# Revit family: ACV Standard Series
name_source: partatom
category: Generic Models
revit_build: Autodesk Revit 2014 (Build: 20130308_1515(x64)
units: mm (PartAtom-declared; Revit-internal decimal feet)

## types (16) — shared parameters
9rp = 9.47 "
Description = BEECO ACV Standard Series
MATERIAL = Iron, Cast
Manufacturer = MIFAB
URL = www.mifab.com

## per-type parameters (varying)
- ACV1.50: 10Hole=0.19 "; 10rp=1.43 "; 1RADIUS=1 "; 1height=0.5 "; 1rib thk=0.21 "; 2radi=2.55 "; 2radi2=1.79 "; 2ribrad=0.05 "; 2ribthk=0.11 "; 3Radius=2 "; 4Height=0.64 "; 4Thk=0.04 "; 5Height=0.9 "; 5inside=0.46 "; 6Outside=0.27 "; 6inside=0.19 "; 6inside2=2.85 "; 7height=0.9 "; 7rp=1.98 "; 7width=0.45 "; 8 HOLE DIST=2.32 "; 8HOLE=0.08 "; 9 HOLE RAD=1.13 "; 9Hole=0.11 "; CutID=0.49 "; Dia.=1.5 "; H=7.31 "; L=9.06 "; R=3.25 "; R RADIUS=0.3 "; R THK=2 "; Radius=0.75 "; W=6 "; W/2=3 "; l1=1.08 "
- ACV2.00: 10Hole=0.25 "; 10rp=1.9 "; 1RADIUS=1.25 "; 1height=0.5 "; 1rib thk=0.29 "; 2radi=2.55 "; 2radi2=1.79 "; 2ribrad=0.05 "; 2ribthk=0.15 "; 3Radius=1.5 "; 4Height=0.85 "; 4Thk=0.05 "; 5Height=1.2 "; 5inside=0.46 "; 6Outside=0.36 "; 6inside=0.25 "; 6inside2=2.75 "; 7height=1.2 "; 7rp=1.94 "; 7width=0.6 "; 8 HOLE DIST=2.32 "; 8HOLE=0.1 "; 9 HOLE RAD=1.5 "; 9Hole=0.15 "; CutID=0.65 "; Dia.=2 "; H=7.31 "; L=9.06 "; R=3.25 "; R RADIUS=0.4 "; R THK=2 "; Radius=1 "; W=6 "; W/2=3 "; l1=1.06 "
- ACV2.50: 10Hole=0.31 "; 10rp=2.38 "; 1RADIUS=1.35 "; 1height=0.95 "; 1rib thk=0.36 "; 2radi=2.55 "; 2radi2=1.79 "; 2ribrad=0.04 "; 2ribthk=0.19 "; 3Radius=1.75 "; 4Height=1.06 "; 4Thk=0.07 "; 5Height=1.5 "; 5inside=0.46 "; 6Outside=0.45 "; 6inside=0.31 "; 6inside2=2.25 "; 7height=1.5 "; 7rp=1.91 "; 7width=0.75 "; 8 HOLE DIST=2.32 "; 8HOLE=0.13 "; 9 HOLE RAD=1.88 "; 9Hole=0.19 "; CutID=0.81 "; Dia.=2.5 "; H=7.31 "; L=12.5 "; R=3.63 "; R RADIUS=0.5 "; R THK=2 "; Radius=1.25 "; W=6 "; W/2=3 "; l1=1.47 "
- ACV3.00: 10Hole=0.38 "; 10rp=2.85 "; 1RADIUS=1.6 "; 1height=1 "; 1rib thk=0.43 "; 2radi=3.35 "; 2radi2=2.35 "; 2ribrad=0.05 "; 2ribthk=0.23 "; 3Radius=3 "; 4Height=1.28 "; 4Thk=0.08 "; 5Height=1.8 "; 5inside=0.6 "; 6Outside=0.55 "; 6inside=0.38 "; 6inside2=2.65 "; 7height=1.8 "; 7rp=2.52 "; 7width=0.9 "; 8 HOLE DIST=3.05 "; 8HOLE=0.15 "; 9 HOLE RAD=2.25 "; 9Hole=0.23 "; CutID=0.98 "; Dia.=3 "; H=9.06 "; L=12.18 "; R=3.94 "; R RADIUS=0.6 "; R THK=1.75 "; Radius=1.5 "; W=7.88 "; W/2=3.94 "; l1=1.42 "
- ACV4.00: 10Hole=0.5 "; 10rp=3.8 "; 1RADIUS=2 "; 1height=0.75 "; 1rib thk=0.57 "; 2radi=3.94 "; 2radi2=2.76 "; 2ribrad=0.06 "; 2ribthk=0.3 "; 3Radius=2.75 "; 4Height=1.7 "; 4Thk=0.1 "; 5Height=2.4 "; 5inside=0.71 "; 6Outside=0.73 "; 6inside=0.5 "; 6inside2=1.6 "; 7height=2.4 "; 7rp=2.93 "; 7width=1.2 "; 8 HOLE DIST=3.58 "; 8HOLE=0.15 "; 9 HOLE RAD=3 "; 9Hole=0.23 "; CutID=1.3 "; Dia.=4 "; H=9.44 "; L=13.75 "; R=4.31 "; R RADIUS=0.8 "; R THK=2 "; Radius=2 "; W=9.25 "; W/2=4.63 "; l1=1.58 "
- ACV6.00: 10Hole=0.75 "; 10rp=5.7 "; 1RADIUS=3 "; 1height=1 "; 1rib thk=0.86 "; 2radi=5.53 "; 2radi2=3.87 "; 2ribrad=0.09 "; 2ribthk=0.45 "; 3Radius=4 "; 4Height=2.55 "; 4Thk=0.16 "; 5Height=3.6 "; 5inside=1 "; 6Outside=1.09 "; 6inside=0.75 "; 6inside2=1.8 "; 7height=3.6 "; 7rp=4.09 "; 7width=1.8 "; 8 HOLE DIST=5.03 "; 8HOLE=0.2 "; 9 HOLE RAD=4.5 "; 9Hole=0.3 "; CutID=1.95 "; Dia.=6 "; H=13 "; L=18.88 "; R=5.63 "; R RADIUS=1.2 "; R THK=2.25 "; Radius=3 "; W=13 "; W/2=6.5 "; l1=2.15 "
- ACV8.00: 10Hole=1 "; 10rp=7.6 "; 1RADIUS=4 "; 1height=1 "; 1rib thk=1.14 "; 2radi=6.94 "; 2radi2=4.86 "; 2ribrad=0.12 "; 2ribthk=0.6 "; 3Radius=5 "; 4Height=3.4 "; 4Thk=0.21 "; 5Height=4.8 "; 5inside=1.25 "; 6Outside=1.45 "; 6inside=1 "; 6inside2=1 "; 7height=4.8 "; 7rp=5.09 "; 7width=2.4 "; 8 HOLE DIST=6.32 "; 8HOLE=0.3 "; 9 HOLE RAD=6 "; 9Hole=0.45 "; CutID=2.6 "; Dia.=8 "; H=15.38 "; L=23.63 "; R=6.75 "; R RADIUS=1.6 "; R THK=2.5 "; Radius=4 "; W=16.31 "; W/2=8.16 "; l1=2.67 "
- ACV10.00: 10Hole=1.25 "; 10rp=9.5 "; 1RADIUS=5 "; 1height=1.5 "; 1rib thk=1.43 "; 2radi=8.8 "; 2radi2=6.16 "; 2ribrad=0.15 "; 2ribthk=0.75 "; 3Radius=7.5 "; 4Height=4.25 "; 4Thk=0.26 "; 5Height=6 "; 5inside=1.58 "; 6Outside=1.82 "; 6inside=1.25 "; 6inside2=2.25 "; 7height=6 "; 7rp=6.47 "; 7width=3 "; 8 HOLE DIST=8.01 "; 8HOLE=0.5 "; 9 HOLE RAD=7.5 "; 9Hole=0.75 "; CutID=3.25 "; Dia.=10 "; H=20.5 "; L=28.75 "; R=8 "; R RADIUS=2 "; R THK=2 "; Radius=5 "; W=20.69 "; W/2=10.35 "; l1=3.24 "
- ACV12.00: 10Hole=1.5 "; 10rp=11.4 "; 1RADIUS=6 "; 1height=1.25 "; 1rib thk=1.71 "; 2radi=10.21 "; 2radi2=7.15 "; 2ribrad=0.18 "; 2ribthk=0.9 "; 3Radius=9 "; 4Height=5.1 "; 4Thk=0.31 "; 5Height=7.2 "; 5inside=1.84 "; 6Outside=2.18 "; 6inside=1.5 "; 6inside2=3.6 "; 7height=7.2 "; 7rp=7.47 "; 7width=3.6 "; 8 HOLE DIST=9.29 "; 8HOLE=0.45 "; 9 HOLE RAD=9 "; 9Hole=0.68 "; CutID=3.9 "; Dia.=12 "; H=25 "; L=33.44 "; R=9 "; R RADIUS=2.4 "; R THK=2.5 "; Radius=6 "; W=24 "; W/2=12 "; l1=3.75 "
- ACV14.00: 10Hole=1.75 "; 10rp=13.3 "; 1RADIUS=7 "; 1height=2 "; 1rib thk=2 "; 2radi=10.21 "; 2radi2=7.15 "; 2ribrad=0.21 "; 2ribthk=1.05 "; 3Radius=9 "; 4Height=5.95 "; 4Thk=0.36 "; 5Height=8.4 "; 5inside=1.84 "; 6Outside=2.55 "; 6inside=1.75 "; 6inside2=2 "; 7height=8.4 "; 7rp=7.32 "; 7width=4.2 "; 8 HOLE DIST=9.29 "; 8HOLE=0.45 "; 9 HOLE RAD=9 "; 9Hole=0.68 "; CutID=4.55 "; Dia.=14 "; H=25 "; L=38.56 "; R=10.69 "; R RADIUS=2.8 "; R THK=2.5 "; Radius=7 "; W=24 "; W/2=12 "; l1=4.32 "
- ACV16.00: 10Hole=2 "; 10rp=15.2 "; 1RADIUS=7.5 "; 1height=2.35 "; 1rib thk=2.29 "; 2radi=14.23 "; 2radi2=9.96 "; 2ribrad=0.24 "; 2ribthk=1.2 "; 3Radius=12 "; 4Height=6.8 "; 4Thk=0.42 "; 5Height=9.6 "; 5inside=2.56 "; 6Outside=2.91 "; 6inside=2 "; 6inside2=4.25 "; 7height=9.6 "; 7rp=10.47 "; 7width=4.8 "; 8 HOLE DIST=12.95 "; 8HOLE=0.6 "; 9 HOLE RAD=12 "; 9Hole=0.9 "; CutID=5.2 "; Dia.=16 "; H=33.63 "; L=43.31 "; R=11.44 "; R RADIUS=3.2 "; R THK=2 "; Radius=8 "; W=33.44 "; W/2=16.72 "; l1=4.84 "
- ACV18.00: 10Hole=2.25 "; 10rp=17.1 "; 1RADIUS=9 "; 1height=2 "; 1rib thk=2.57 "; 2radi=14.23 "; 2radi2=9.96 "; 2ribrad=0.27 "; 2ribthk=1.35 "; 3Radius=13 "; 4Height=7.65 "; 4Thk=0.47 "; 5Height=10.8 "; 5inside=2.56 "; 6Outside=3.27 "; 6inside=2.25 "; 6inside2=3 "; 7height=10.8 "; 7rp=10.32 "; 7width=5.4 "; 8 HOLE DIST=12.95 "; 8HOLE=0.65 "; 9 HOLE RAD=12 "; 9Hole=0.98 "; CutID=5.85 "; Dia.=18 "; H=33.63 "; L=47.25 "; R=12.18 "; R RADIUS=3.6 "; R THK=3 "; Radius=9 "; W=33.44 "; W/2=16.72 "; l1=5.26 "
- ACV20.00: 10Hole=2.5 "; 10rp=19 "; 1RADIUS=10 "; 1height=2.25 "; 1rib thk=2.86 "; 2radi=14.23 "; 2radi2=9.96 "; 2ribrad=0.3 "; 2ribthk=1.5 "; 3Radius=14 "; 4Height=8.5 "; 4Thk=0.52 "; 5Height=12 "; 5inside=2.56 "; 6Outside=3.64 "; 6inside=2.5 "; 6inside2=1.5 "; 7height=12 "; 7rp=10.17 "; 7width=6 "; 8 HOLE DIST=12.95 "; 8HOLE=0.7 "; 9 HOLE RAD=12.5 "; 9Hole=1.05 "; CutID=6.5 "; Dia.=20 "; H=33.63 "; L=49.18 "; R=14.06 "; R RADIUS=4 "; R THK=3.5 "; Radius=10 "; W=33.44 "; W/2=16.72 "; l1=5.43 "
- ACV24.00: 10Hole=3 "; 10rp=22.8 "; 1RADIUS=12 "; 1height=2.5 "; 1rib thk=3.43 "; 2radi=18.43 "; 2radi2=12.9 "; 2ribrad=0.36 "; 2ribthk=1.8 "; 3Radius=18 "; 4Height=10.2 "; 4Thk=0.62 "; 5Height=14.4 "; 5inside=3.32 "; 6Outside=4.36 "; 6inside=3 "; 6inside2=21 "; 7height=14.4 "; 7rp=13.31 "; 7width=7.2 "; 8 HOLE DIST=16.77 "; 8HOLE=0.8 "; 9 HOLE RAD=15 "; 9Hole=1.2 "; CutID=7.8 "; Dia.=24 "; H=61.94 "; L=57.06 "; R=19.31 "; R RADIUS=4.8 "; R THK=6 "; Radius=12 "; W=43.31 "; W/2=21.66 "; l1=6.28 "
- ACV28.00: 10Hole=3.5 "; 10rp=26.6 "; 1RADIUS=14 "; 1height=3 "; 1rib thk=4 "; 2radi=18.43 "; 2radi2=12.9 "; 2ribrad=0.42 "; 2ribthk=2.1 "; 3Radius=18 "; 4Height=11.9 "; 4Thk=0.73 "; 5Height=16.8 "; 5inside=3.32 "; 6Outside=5.09 "; 6inside=3.5 "; 6inside2=22 "; 7height=16.8 "; 7rp=13.01 "; 7width=8.4 "; 8 HOLE DIST=16.77 "; 8HOLE=0.85 "; 9 HOLE RAD=16.5 "; 9Hole=1.28 "; CutID=9.1 "; Dia.=28 "; H=65.94 "; L=64.94 "; R=19.63 "; R RADIUS=5.6 "; R THK=5 "; Radius=14 "; W=43.31 "; W/2=21.66 "; l1=7.12 "
- ACV32.00: 10Hole=4 "; 10rp=30.4 "; 1RADIUS=15 "; 1height=3 "; 1rib thk=4.57 "; 2radi=18.27 "; 2radi2=12.79 "; 2ribrad=0.48 "; 2ribthk=2.4 "; 3Radius=18.5 "; 4Height=13.6 "; 4Thk=0.83 "; 5Height=19.2 "; 5inside=3.29 "; 6Outside=5.82 "; 6inside=4 "; 6inside2=19 "; 7height=19.2 "; 7rp=12.58 "; 7width=9.6 "; 8 HOLE DIST=16.63 "; 8HOLE=0.9 "; 9 HOLE RAD=18 "; 9Hole=1.35 "; CutID=10.4 "; Dia.=32 "; H=65.94 "; L=72.88 "; R=23.75 "; R RADIUS=6.4 "; R THK=7.5 "; Radius=16 "; W=42.94 "; W/2=21.47 "; l1=7.97 "

note: column(s) folded — value = type name in every type: Model
